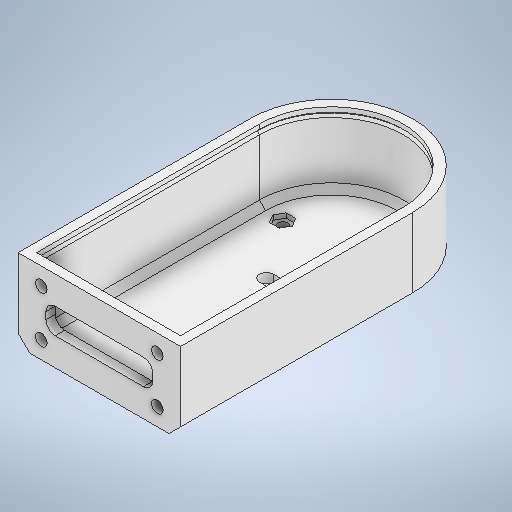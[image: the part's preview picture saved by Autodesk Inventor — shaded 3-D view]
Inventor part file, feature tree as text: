
AUTODESK INVENTOR PART (.ipt)
format: ipt  version: 2025.2 (Build 292293000, 293)  size: 366,592 bytes
history: native  units: mm
features: sketch x6, extrude x4, plane x2, chamfer x1, shell x1, sweep x1, fillet x1
ambient origin geometry x8: Origin, YZ Plane, XZ Plane, XY Plane, X Axis, Y Axis, Z Axis, Center Point
bodies: Solid1 (feature_tree)
feature tree (16):
  extrude  "Extrusion1"  Depth=4.0mm
  chamfer  "Chamfer1"  Distance=35.0mm
  shell  "Shell1"  Thickness=4.0mm
  extrude  "Extrusion2"  Depth=12.0mm
  plane  "Work Plane2"
  sketch  "Sketch4"  dims[d9=50.0mm d10=20.0mm]
  plane  "Work Plane3"
  sweep  "Sweep1"
  extrude  "Extrusion5"  TaperAngle=0.0deg  [1 undecoded]
  extrude  "Extrusion6"  Depth=1.0mm
  fillet  "Fillet1"  [1 undecoded]
  sketch  "Sketch1"  dims[d0=70.0mm d1=100.0mm d2=35.0mm d3=0.0mm d4=4.0mm]
  sketch  "Sketch2"  dims[d7=12.0mm d8=5.0mm]
  sketch  "Sketch5"  dims[d11=50.0mm d12=0.0mm]
  sketch  "Sketch6"  dims[d28=-3.0mm d29=1.0mm d30=45.0deg]
  sketch  "Sketch7"  dims[d31=0.0mm d32=0.0mm d33=4.3mm d34=42.0mm d35=50.0mm d36=0.0mm d37=6.0mm d38=6.0mm d39=25.0mm d40=7.2mm d41=2.0mm d42=0.0mm d43=5.0mm d44=2.0mm d45=45.0deg d46=4.0mm]
note: 2 required parameter values undecoded (feature->parameter linkage not recoverable at this tier; creation-order binding heuristic only, values carry confidence <= 0.55)
